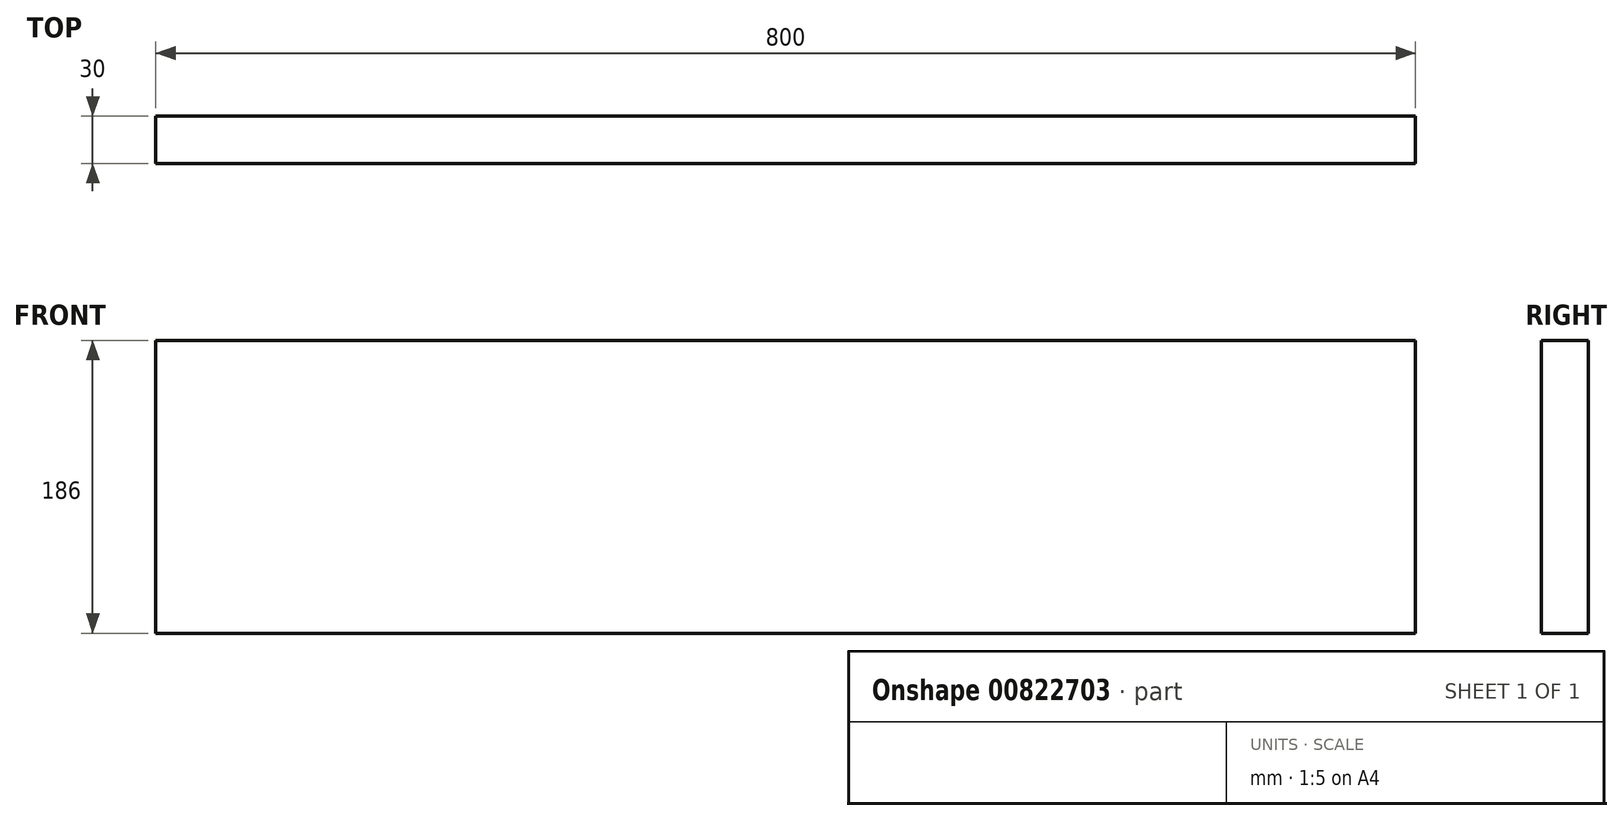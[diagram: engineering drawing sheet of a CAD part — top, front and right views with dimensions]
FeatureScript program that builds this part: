
annotation { "Feature Type Name" : "Feature", "Feature Type Description" : "" }
export const myFeature = defineFeature(function(context is Context, id is Id, definition is map)
    precondition{}
    {
        {
            var Q0;
            Q0=qCreatedBy(makeId("Front.planeOp"),FACE);
            var sketch = newSketch(context, id + "F0", { "sketchPlane" : qUnion([Q0])});
            skLineSegment(sketch, "E0.bottom", {"start": v(0, 0) * mm, "end": v(800, 0) * mm});
            skLineSegment(sketch, "E0.top", {"start": v(0, 186) * mm, "end": v(800, 186) * mm});
            skLineSegment(sketch, "E0.left", {"start": v(0, 0) * mm, "end": v(0, 186) * mm});
            skLineSegment(sketch, "E0.right", {"start": v(800, 0) * mm, "end": v(800, 186) * mm});
            skSolve(sketch);
        }
        {
            var Q0;
            Q0=makeQuery(id+"F0.imprint","IMPRINT",FACE,{"disambiguationData":[TD([[makeQuery(id+"F0.imprint","IMPRINT",EDGE,{"derivedFrom":sQuery(id+"F0.wireOp",EDGE,"E0.bottom")}),1.0]])]});
            extrude(context, id + "F1", {"entities" : qUnion([Q0]), "depth" : 30 * mm, "offsetDistance" : 25 * mm});
        }
    });
